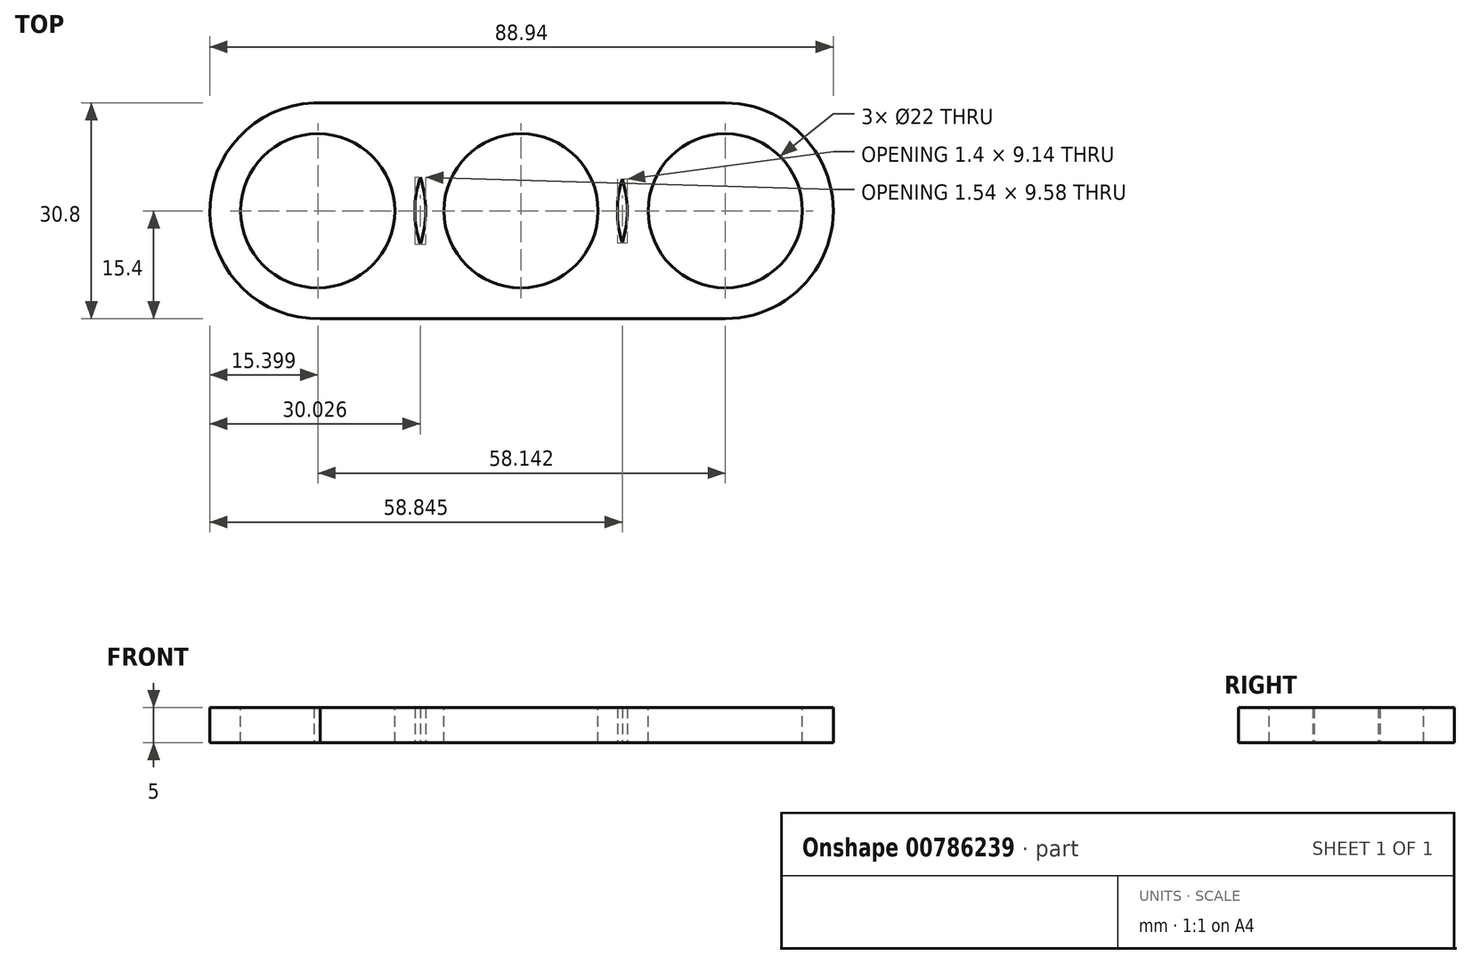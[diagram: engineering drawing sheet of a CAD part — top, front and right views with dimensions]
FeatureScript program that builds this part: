
annotation { "Feature Type Name" : "Feature", "Feature Type Description" : "" }
export const myFeature = defineFeature(function(context is Context, id is Id, definition is map)
    precondition{}
    {
        {
            var Q0;
            Q0=qCreatedBy(makeId("Top.planeOp"),FACE);
            var sketch = newSketch(context, id + "F0", { "sketchPlane" : qUnion([Q0])});
            skCircle(sketch, "E0", {"center": v(0, 0) * mm, "radius": 15.15 * mm});
            skCircle(sketch, "E1", {"center": v(-29, 0) * mm, "radius": 15.4 * mm});
            skCircle(sketch, "E2", {"center": v(29.14, 0) * mm, "radius": 15.4 * mm});
            skLineSegment(sketch, "E3", {"start": v(-29.55, 15.39) * mm, "end": v(29.14, 15.4) * mm});
            skLineSegment(sketch, "E4", {"start": v(-28.63, -15.4) * mm, "end": v(29.14, -15.4) * mm});
            skSolve(sketch);
        }
        {
            var Q0;
            {var subQ0=sQuery(id+"F0.wireOp",EDGE,"E1");var subQ1=sQuery(id+"F0.wireOp",EDGE,"E0");var subQ2=makeQuery(id+"F0.imprint","INTERSECT",VERTEX,{"disambiguationData":[OD(0.0)],"derivedFrom":[subQ1,subQ0]});Q0=makeQuery(id+"F0.imprint","IMPRINT",FACE,{"disambiguationData":[TD([[makeQuery(id+"F0.imprint","IMPRINT",EDGE,{"disambiguationData":[TD([[subQ2,1.0]])],"derivedFrom":subQ1}),1.0]])]});}
            var Q1;
            {var subQ0=sQuery(id+"F0.wireOp",EDGE,"E1");var subQ2=sQuery(id+"F0.wireOp",EDGE,"E0");var subQ6=makeQuery(id+"F0.imprint","INTERSECT",VERTEX,{"disambiguationData":[OD(0.0)],"derivedFrom":[subQ2,subQ0]});Q1=makeQuery(id+"F0.imprint","IMPRINT",FACE,{"disambiguationData":[TD([[makeQuery(id+"F0.imprint","IMPRINT",EDGE,{"disambiguationData":[TD([[subQ6,-1.0]])],"derivedFrom":subQ2}),-1.0]])]});}
            var Q2;
            {var subQ5=sQuery(id+"F0.wireOp",EDGE,"E4");Q2=makeQuery(id+"F0.imprint","IMPRINT",FACE,{"disambiguationData":[TD([[makeQuery(id+"F0.imprint","IMPRINT",EDGE,{"derivedFrom":subQ5}),1.0]])]});}
            var Q3;
            {var subQ0=sQuery(id+"F0.wireOp",EDGE,"E1");var subQ1=sQuery(id+"F0.wireOp",EDGE,"E0");var subQ2=makeQuery(id+"F0.imprint","INTERSECT",VERTEX,{"disambiguationData":[OD(0.0)],"derivedFrom":[subQ1,subQ0]});Q3=makeQuery(id+"F0.imprint","IMPRINT",FACE,{"disambiguationData":[TD([[makeQuery(id+"F0.imprint","IMPRINT",EDGE,{"disambiguationData":[TD([[subQ2,1.0]])],"derivedFrom":subQ1}),-1.0]])]});}
            var Q4;
            {var subQ0=sQuery(id+"F0.wireOp",EDGE,"E2");var subQ1=sQuery(id+"F0.wireOp",EDGE,"E0");var subQ2=makeQuery(id+"F0.imprint","INTERSECT",VERTEX,{"disambiguationData":[OD(0.0)],"derivedFrom":[subQ1,subQ0]});Q4=makeQuery(id+"F0.imprint","IMPRINT",FACE,{"disambiguationData":[TD([[makeQuery(id+"F0.imprint","IMPRINT",EDGE,{"disambiguationData":[TD([[subQ2,1.0]])],"derivedFrom":subQ1}),-1.0]])]});}
            extrude(context, id + "F1", {"entities" : qUnion([Q0, Q1, Q2, Q3, Q4]), "depth" : 5 * mm, "offsetDistance" : 25 * mm});
        }
        {
            var Q0;
            Q0=makeQuery(id+"F1.opExtrude","CAP_FACE",FACE,{"disambiguationData":[OSD([sQuery(id+"F0.wireOp",EDGE,"E0"),sQuery(id+"F0.wireOp",EDGE,"E1"),sQuery(id+"F0.wireOp",EDGE,"E2"),sQuery(id+"F0.wireOp",EDGE,"E3"),sQuery(id+"F0.wireOp",EDGE,"E4")])],"isStart":false});
            var sketch = newSketch(context, id + "F2", { "sketchPlane" : qUnion([Q0])});
            skCircle(sketch, "E5", {"center": v(-29, 0) * mm, "radius": 11.31 * mm});
            skCircle(sketch, "E6", {"center": v(0, 0) * mm, "radius": 11.29 * mm});
            skCircle(sketch, "E7", {"center": v(29.14, 0) * mm, "radius": 11.26 * mm});
            skSolve(sketch);
        }
        {
            var Q0;
            Q0=sQuery(id+"F2.wireOp",VERTEX,"E5.center");
            var Q1;
            Q1=makeQuery(id+"F1.opExtrude","SWEPT_BODY",BODY,{"disambiguationData":[OSD([sQuery(id+"F0.wireOp",EDGE,"E0"),sQuery(id+"F0.wireOp",EDGE,"E1"),sQuery(id+"F0.wireOp",EDGE,"E2"),sQuery(id+"F0.wireOp",EDGE,"E3"),sQuery(id+"F0.wireOp",EDGE,"E4")])]});
            hole(context, id + "F3", {"style" : HoleStyle.SIMPLE, "endStyle" : HoleEndStyle.THROUGH, "holeDiameter" : 22 * mm, "majorDiameter" : 5 * mm, "isTappedThrough" : true, "tappedDepth" : 12 * mm, "tapClearance" : 3, "locations" : qUnion([Q0]), "scope" : qUnion([Q1])});
        }
        {
            var Q0;
            Q0=makeQuery(id+"F1.opExtrude","CAP_FACE",FACE,{"disambiguationData":[OSD([sQuery(id+"F0.wireOp",EDGE,"E0"),sQuery(id+"F0.wireOp",EDGE,"E1"),sQuery(id+"F0.wireOp",EDGE,"E2"),sQuery(id+"F0.wireOp",EDGE,"E3"),sQuery(id+"F0.wireOp",EDGE,"E4")])],"isStart":false});
            var sketch = newSketch(context, id + "F4", { "sketchPlane" : qUnion([Q0])});
            skCircle(sketch, "E8", {"center": v(0, 0) * mm, "radius": 4.89 * mm});
            skSolve(sketch);
        }
        {
            var Q0;
            Q0=sQuery(id+"F4.wireOp",VERTEX,"E8.center");
            var Q1;
            Q1=makeQuery(id+"F1.opExtrude","SWEPT_BODY",BODY,{"disambiguationData":[OSD([sQuery(id+"F0.wireOp",EDGE,"E0"),sQuery(id+"F0.wireOp",EDGE,"E1"),sQuery(id+"F0.wireOp",EDGE,"E2"),sQuery(id+"F0.wireOp",EDGE,"E3"),sQuery(id+"F0.wireOp",EDGE,"E4")])]});
            hole(context, id + "F5", {"style" : HoleStyle.SIMPLE, "endStyle" : HoleEndStyle.THROUGH, "holeDiameter" : 22 * mm, "majorDiameter" : 5 * mm, "isTappedThrough" : true, "tappedDepth" : 12 * mm, "tapClearance" : 3, "locations" : qUnion([Q0]), "scope" : qUnion([Q1])});
        }
        {
            var Q0;
            Q0=makeQuery(id+"F1.opExtrude","CAP_FACE",FACE,{"disambiguationData":[OSD([sQuery(id+"F0.wireOp",EDGE,"E0"),sQuery(id+"F0.wireOp",EDGE,"E1"),sQuery(id+"F0.wireOp",EDGE,"E2"),sQuery(id+"F0.wireOp",EDGE,"E3"),sQuery(id+"F0.wireOp",EDGE,"E4")])],"isStart":false});
            var sketch = newSketch(context, id + "F6", { "sketchPlane" : qUnion([Q0])});
            skCircle(sketch, "E9", {"center": v(29.14, 0) * mm, "radius": 11.17 * mm});
            skSolve(sketch);
        }
        {
            var Q0;
            Q0=sQuery(id+"F6.wireOp",VERTEX,"E9.center");
            var Q1;
            Q1=makeQuery(id+"F1.opExtrude","SWEPT_BODY",BODY,{"disambiguationData":[OSD([sQuery(id+"F0.wireOp",EDGE,"E0"),sQuery(id+"F0.wireOp",EDGE,"E1"),sQuery(id+"F0.wireOp",EDGE,"E2"),sQuery(id+"F0.wireOp",EDGE,"E3"),sQuery(id+"F0.wireOp",EDGE,"E4")])]});
            hole(context, id + "F7", {"style" : HoleStyle.SIMPLE, "endStyle" : HoleEndStyle.THROUGH, "holeDiameter" : 22 * mm, "majorDiameter" : 5 * mm, "isTappedThrough" : true, "tappedDepth" : 12 * mm, "tapClearance" : 3, "locations" : qUnion([Q0]), "scope" : qUnion([Q1])});
        }
    });
